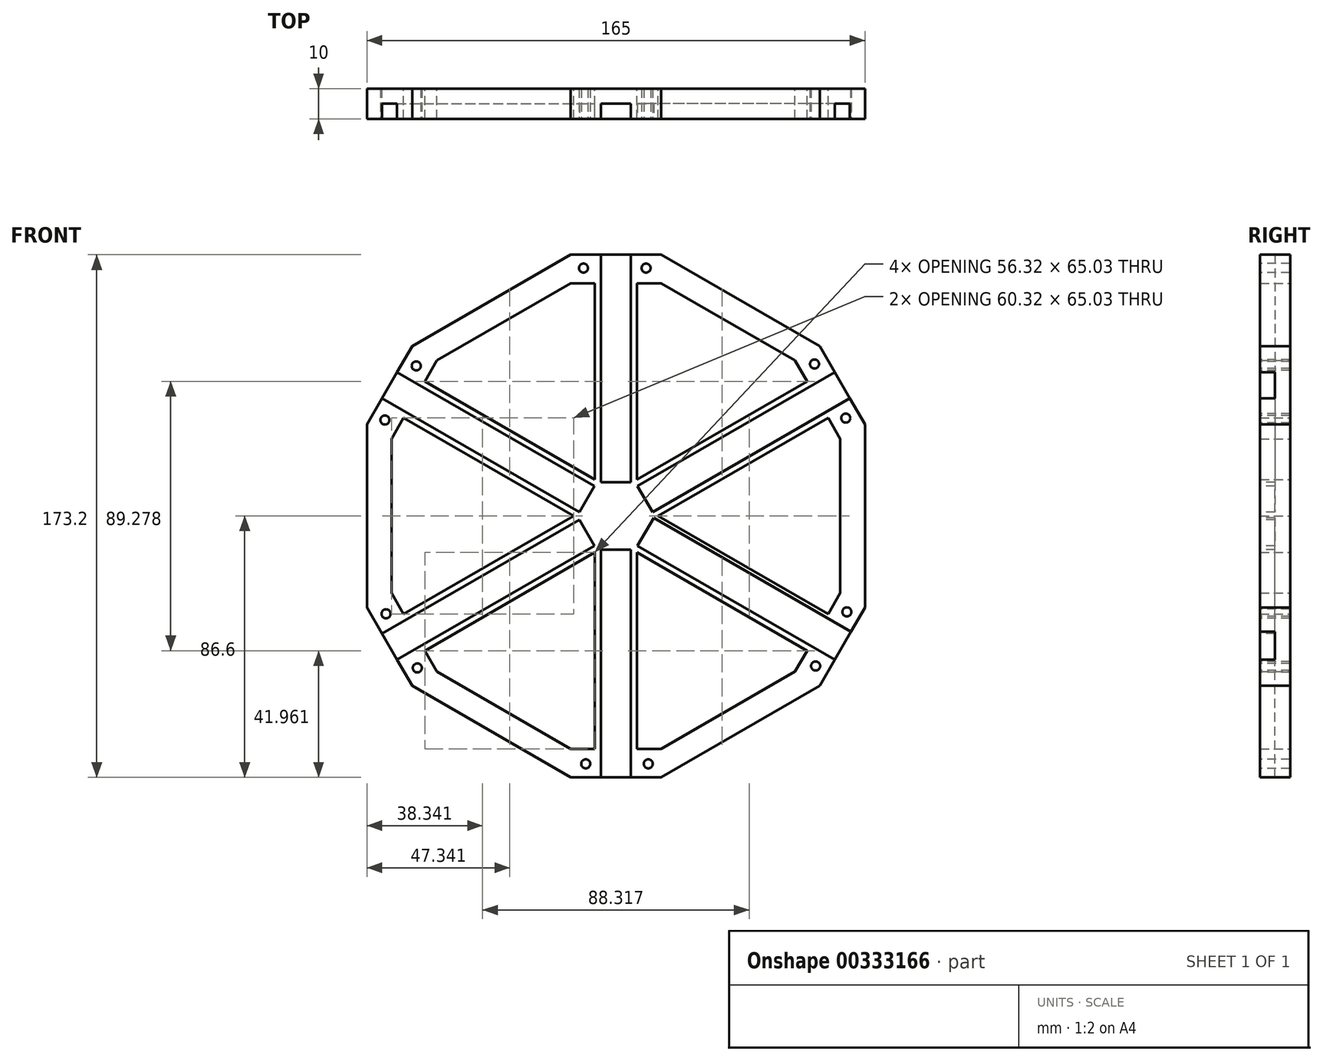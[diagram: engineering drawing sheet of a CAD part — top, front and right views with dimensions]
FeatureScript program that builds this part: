
annotation { "Feature Type Name" : "Feature", "Feature Type Description" : "" }
export const myFeature = defineFeature(function(context is Context, id is Id, definition is map)
    precondition{}
    {
        {
            var Q0;
            Q0=qCreatedBy(makeId("Front.planeOp"),FACE);
            var sketch = newSketch(context, id + "F0", { "sketchPlane" : qUnion([Q0])});
            skCircle(sketch, "E0.cCircle", {"center": v(0, 0) * mm, "radius": 86.6 * mm, "construction": true});
            skLineSegment(sketch, "E0.0", {"start": v(-50, 86.6) * mm, "end": v(50, 86.6) * mm});
            skLineSegment(sketch, "E0.1", {"start": v(50, 86.6) * mm, "end": v(100, 0) * mm});
            skLineSegment(sketch, "E0.2", {"start": v(100, 0) * mm, "end": v(50, -86.6) * mm});
            skLineSegment(sketch, "E0.3", {"start": v(50, -86.6) * mm, "end": v(-50, -86.6) * mm});
            skLineSegment(sketch, "E0.4", {"start": v(-50, -86.6) * mm, "end": v(-100, 0) * mm});
            skLineSegment(sketch, "E0.5", {"start": v(-100, 0) * mm, "end": v(-50, 86.6) * mm});
            skPoint(sketch, "E0.0.midPoint", {"position": v(0, 86.6) * mm});
            skLineSegment(sketch, "E1", {"start": v(-15, 86.6) * mm, "end": v(-15, 77.15) * mm});
            skLineSegment(sketch, "E2", {"start": v(-15, 77.15) * mm, "end": v(-7, 77.15) * mm});
            skLineSegment(sketch, "E3", {"start": v(-7, 77.15) * mm, "end": v(-7, 12.12) * mm});
            skLineSegment(sketch, "E4.MirrorCS", {"start": v(7, 77.15) * mm, "end": v(7, 12.12) * mm});
            skLineSegment(sketch, "E5.MirrorCS", {"start": v(15, 77.15) * mm, "end": v(7, 77.15) * mm});
            skLineSegment(sketch, "E6.MirrorCS", {"start": v(15, 86.6) * mm, "end": v(15, 77.15) * mm});
            skLineSegment(sketch, "E7.1.0", {"start": v(-82.5, 30.31) * mm, "end": v(-74.32, 25.59) * mm});
            skLineSegment(sketch, "E7.1.1", {"start": v(-70.32, 32.51) * mm, "end": v(-14, 0) * mm});
            skLineSegment(sketch, "E7.1.2", {"start": v(-63.32, 44.64) * mm, "end": v(-7, 12.12) * mm});
            skLineSegment(sketch, "E7.1.3", {"start": v(-67.5, 56.3) * mm, "end": v(-59.32, 51.57) * mm});
            skPoint(sketch, "E7.1.4", {"position": v(-75, 43.3) * mm});
            skLineSegment(sketch, "E7.1.5", {"start": v(-74.32, 25.59) * mm, "end": v(-70.32, 32.51) * mm});
            skLineSegment(sketch, "E7.1.6", {"start": v(-59.32, 51.57) * mm, "end": v(-63.32, 44.64) * mm});
            skLineSegment(sketch, "E7.2.0", {"start": v(-67.5, -56.3) * mm, "end": v(-59.32, -51.57) * mm});
            skLineSegment(sketch, "E7.2.1", {"start": v(-63.32, -44.64) * mm, "end": v(-7, -12.12) * mm});
            skLineSegment(sketch, "E7.2.2", {"start": v(-70.32, -32.51) * mm, "end": v(-14, 0) * mm});
            skLineSegment(sketch, "E7.2.3", {"start": v(-82.5, -30.31) * mm, "end": v(-74.32, -25.59) * mm});
            skPoint(sketch, "E7.2.4", {"position": v(-75, -43.3) * mm});
            skLineSegment(sketch, "E7.2.5", {"start": v(-59.32, -51.57) * mm, "end": v(-63.32, -44.64) * mm});
            skLineSegment(sketch, "E7.2.6", {"start": v(-74.32, -25.59) * mm, "end": v(-70.32, -32.51) * mm});
            skLineSegment(sketch, "E7.3.0", {"start": v(15, -86.6) * mm, "end": v(15, -77.15) * mm});
            skLineSegment(sketch, "E7.3.1", {"start": v(7, -77.15) * mm, "end": v(7, -12.12) * mm});
            skLineSegment(sketch, "E7.3.2", {"start": v(-7, -77.15) * mm, "end": v(-7, -12.12) * mm});
            skLineSegment(sketch, "E7.3.3", {"start": v(-15, -86.6) * mm, "end": v(-15, -77.15) * mm});
            skPoint(sketch, "E7.3.4", {"position": v(0, -86.6) * mm});
            skLineSegment(sketch, "E7.3.5", {"start": v(15, -77.15) * mm, "end": v(7, -77.15) * mm});
            skLineSegment(sketch, "E7.3.6", {"start": v(-15, -77.15) * mm, "end": v(-7, -77.15) * mm});
            skLineSegment(sketch, "E7.4.0", {"start": v(82.5, -30.31) * mm, "end": v(74.32, -25.59) * mm});
            skLineSegment(sketch, "E7.4.1", {"start": v(70.32, -32.51) * mm, "end": v(14, 0) * mm});
            skLineSegment(sketch, "E7.4.2", {"start": v(63.32, -44.64) * mm, "end": v(7, -12.12) * mm});
            skLineSegment(sketch, "E7.4.3", {"start": v(67.5, -56.3) * mm, "end": v(59.32, -51.57) * mm});
            skPoint(sketch, "E7.4.4", {"position": v(75, -43.3) * mm});
            skLineSegment(sketch, "E7.4.5", {"start": v(74.32, -25.59) * mm, "end": v(70.32, -32.51) * mm});
            skLineSegment(sketch, "E7.4.6", {"start": v(59.32, -51.57) * mm, "end": v(63.32, -44.64) * mm});
            skLineSegment(sketch, "E7.5.0", {"start": v(67.5, 56.3) * mm, "end": v(59.32, 51.57) * mm});
            skLineSegment(sketch, "E7.5.1", {"start": v(63.32, 44.64) * mm, "end": v(7, 12.12) * mm});
            skLineSegment(sketch, "E7.5.2", {"start": v(70.32, 32.51) * mm, "end": v(14, 0) * mm});
            skLineSegment(sketch, "E7.5.3", {"start": v(82.5, 30.31) * mm, "end": v(74.32, 25.59) * mm});
            skPoint(sketch, "E7.5.4", {"position": v(75, 43.3) * mm});
            skLineSegment(sketch, "E7.5.5", {"start": v(59.32, 51.57) * mm, "end": v(63.32, 44.64) * mm});
            skLineSegment(sketch, "E7.5.6", {"start": v(74.32, 25.59) * mm, "end": v(70.32, 32.51) * mm});
            skPoint(sketch, "E8.orphan", {"position": v(-3.5, 6.06) * mm});
            skPoint(sketch, "E9.orphan", {"position": v(-7, 0) * mm});
            skPoint(sketch, "E10.orphan", {"position": v(3.5, 6.06) * mm});
            skPoint(sketch, "E11.trimOffspring.end.orphan", {"position": v(7, 0) * mm});
            skPoint(sketch, "E12.orphan", {"position": v(3.5, -6.06) * mm});
            skLineSegment(sketch, "E13", {"start": v(-15, -77.15) * mm, "end": v(-59.32, -51.57) * mm});
            skLineSegment(sketch, "E14", {"start": v(-74.32, -25.59) * mm, "end": v(-74.32, 25.59) * mm});
            skLineSegment(sketch, "E15", {"start": v(-59.32, 51.57) * mm, "end": v(-15, 77.15) * mm});
            skLineSegment(sketch, "E16", {"start": v(15, 77.15) * mm, "end": v(59.32, 51.57) * mm});
            skLineSegment(sketch, "E17", {"start": v(74.32, 25.59) * mm, "end": v(74.32, -25.59) * mm});
            skLineSegment(sketch, "E18", {"start": v(59.32, -51.57) * mm, "end": v(15, -77.15) * mm});
            skLineSegment(sketch, "E19", {"start": v(15, -86.6) * mm, "end": v(67.5, -56.3) * mm});
            skLineSegment(sketch, "E20", {"start": v(82.5, -30.31) * mm, "end": v(82.5, 30.31) * mm});
            skLineSegment(sketch, "E21", {"start": v(67.5, 56.3) * mm, "end": v(15, 86.6) * mm});
            skLineSegment(sketch, "E22", {"start": v(-15, 86.6) * mm, "end": v(-67.5, 56.3) * mm});
            skLineSegment(sketch, "E23", {"start": v(-82.5, 30.31) * mm, "end": v(-82.5, -30.31) * mm});
            skLineSegment(sketch, "E24", {"start": v(-67.5, -56.3) * mm, "end": v(-15, -86.6) * mm});
            skSolve(sketch);
        }
        {
            var Q0;
            {var subQ9=sQuery(id+"F0.wireOp",EDGE,"E1");Q0=makeQuery(id+"F0.imprint","IMPRINT",FACE,{"disambiguationData":[TD([[makeQuery(id+"F0.imprint","IMPRINT",EDGE,{"derivedFrom":subQ9}),1.0]])]});}
            var Q1;
            Q1=makeQuery(id+"F0.imprint","IMPRINT",FACE,{"disambiguationData":[TD([[makeQuery(id+"F0.imprint","IMPRINT",EDGE,{"derivedFrom":sQuery(id+"F0.wireOp",EDGE,"E7.2.0")}),-1.0]])]});
            var Q2;
            Q2=makeQuery(id+"F0.imprint","IMPRINT",FACE,{"disambiguationData":[TD([[makeQuery(id+"F0.imprint","IMPRINT",EDGE,{"derivedFrom":sQuery(id+"F0.wireOp",EDGE,"E7.1.0")}),-1.0]])]});
            var Q3;
            Q3=makeQuery(id+"F0.imprint","IMPRINT",FACE,{"disambiguationData":[TD([[makeQuery(id+"F0.imprint","IMPRINT",EDGE,{"derivedFrom":sQuery(id+"F0.wireOp",EDGE,"E1")}),-1.0]])]});
            var Q4;
            Q4=makeQuery(id+"F0.imprint","IMPRINT",FACE,{"disambiguationData":[TD([[makeQuery(id+"F0.imprint","IMPRINT",EDGE,{"derivedFrom":sQuery(id+"F0.wireOp",EDGE,"E6.MirrorCS")}),1.0]])]});
            var Q5;
            Q5=makeQuery(id+"F0.imprint","IMPRINT",FACE,{"disambiguationData":[TD([[makeQuery(id+"F0.imprint","IMPRINT",EDGE,{"derivedFrom":sQuery(id+"F0.wireOp",EDGE,"E7.4.0")}),-1.0]])]});
            var Q6;
            Q6=makeQuery(id+"F0.imprint","IMPRINT",FACE,{"disambiguationData":[TD([[makeQuery(id+"F0.imprint","IMPRINT",EDGE,{"derivedFrom":sQuery(id+"F0.wireOp",EDGE,"E7.3.0")}),-1.0]])]});
            extrude(context, id + "F1", {"entities" : qUnion([Q0, Q1, Q2, Q3, Q4, Q5, Q6]), "depth" : 10 * mm});
        }
        {
            var Q0;
            Q0=makeQuery(id+"F1.opExtrude","CAP_FACE",FACE,{"disambiguationData":[OSD([sQuery(id+"F0.wireOp",EDGE,"E0.0"),sQuery(id+"F0.wireOp",EDGE,"E0.1"),sQuery(id+"F0.wireOp",EDGE,"E0.2"),sQuery(id+"F0.wireOp",EDGE,"E0.3"),sQuery(id+"F0.wireOp",EDGE,"E0.4"),sQuery(id+"F0.wireOp",EDGE,"E0.5"),sQuery(id+"F0.wireOp",EDGE,"E1"),sQuery(id+"F0.wireOp",EDGE,"E2"),sQuery(id+"F0.wireOp",EDGE,"E3"),sQuery(id+"F0.wireOp",EDGE,"E4.MirrorCS"),sQuery(id+"F0.wireOp",EDGE,"E5.MirrorCS"),sQuery(id+"F0.wireOp",EDGE,"E6.MirrorCS"),sQuery(id+"F0.wireOp",EDGE,"E7.1.0"),sQuery(id+"F0.wireOp",EDGE,"E7.1.1"),sQuery(id+"F0.wireOp",EDGE,"E7.1.2"),sQuery(id+"F0.wireOp",EDGE,"E7.1.3"),sQuery(id+"F0.wireOp",EDGE,"E7.1.5"),sQuery(id+"F0.wireOp",EDGE,"E7.1.6"),sQuery(id+"F0.wireOp",EDGE,"E7.2.0"),sQuery(id+"F0.wireOp",EDGE,"E7.2.1"),sQuery(id+"F0.wireOp",EDGE,"E7.2.2"),sQuery(id+"F0.wireOp",EDGE,"E7.2.3"),sQuery(id+"F0.wireOp",EDGE,"E7.2.5"),sQuery(id+"F0.wireOp",EDGE,"E7.2.6"),sQuery(id+"F0.wireOp",EDGE,"E7.3.0"),sQuery(id+"F0.wireOp",EDGE,"E7.3.1"),sQuery(id+"F0.wireOp",EDGE,"E7.3.2"),sQuery(id+"F0.wireOp",EDGE,"E7.3.3"),sQuery(id+"F0.wireOp",EDGE,"E7.3.5"),sQuery(id+"F0.wireOp",EDGE,"E7.3.6"),sQuery(id+"F0.wireOp",EDGE,"E7.4.0"),sQuery(id+"F0.wireOp",EDGE,"E7.4.1"),sQuery(id+"F0.wireOp",EDGE,"E7.4.2"),sQuery(id+"F0.wireOp",EDGE,"E7.4.3"),sQuery(id+"F0.wireOp",EDGE,"E7.4.5"),sQuery(id+"F0.wireOp",EDGE,"E7.4.6"),sQuery(id+"F0.wireOp",EDGE,"E7.5.0"),sQuery(id+"F0.wireOp",EDGE,"E7.5.1"),sQuery(id+"F0.wireOp",EDGE,"E7.5.2"),sQuery(id+"F0.wireOp",EDGE,"E7.5.3"),sQuery(id+"F0.wireOp",EDGE,"E7.5.5"),sQuery(id+"F0.wireOp",EDGE,"E7.5.6")])],"isStart":false});
            var sketch = newSketch(context, id + "F2", { "sketchPlane" : qUnion([Q0])});
            skLineSegment(sketch, "E25.bottom", {"start": v(-5, 86.6) * mm, "end": v(5, 86.6) * mm});
            skLineSegment(sketch, "E25.left", {"start": v(-5, 86.6) * mm, "end": v(-5, 8.66) * mm});
            skLineSegment(sketch, "E25.right", {"start": v(5, 86.6) * mm, "end": v(5, 8.66) * mm});
            skLineSegment(sketch, "E26.1.1", {"start": v(-114.84, 60.53) * mm, "end": v(-10, 0) * mm});
            skLineSegment(sketch, "E26.1.2", {"start": v(-109.84, 69.2) * mm, "end": v(-5, 8.66) * mm});
            skLineSegment(sketch, "E26.1.3", {"start": v(-114.84, 60.53) * mm, "end": v(-109.84, 69.2) * mm});
            skLineSegment(sketch, "E26.2.1", {"start": v(-136.83, -84.77) * mm, "end": v(-5, -8.66) * mm});
            skLineSegment(sketch, "E26.2.2", {"start": v(-141.83, -76.11) * mm, "end": v(-10, 0) * mm});
            skLineSegment(sketch, "E26.2.3", {"start": v(-136.83, -84.77) * mm, "end": v(-141.83, -76.11) * mm});
            skLineSegment(sketch, "E26.3.1", {"start": v(5, -109.05) * mm, "end": v(5, -8.66) * mm});
            skLineSegment(sketch, "E26.3.2", {"start": v(-5, -109.05) * mm, "end": v(-5, -8.66) * mm});
            skLineSegment(sketch, "E26.3.3", {"start": v(5, -109.05) * mm, "end": v(-5, -109.05) * mm});
            skLineSegment(sketch, "E26.4.1", {"start": v(112.24, -58.19) * mm, "end": v(10.73, 0.42) * mm});
            skLineSegment(sketch, "E26.4.2", {"start": v(106.88, -67.48) * mm, "end": v(5, -8.66) * mm});
            skLineSegment(sketch, "E26.4.3", {"start": v(112.24, -58.19) * mm, "end": v(106.88, -67.48) * mm});
            skLineSegment(sketch, "E26.5.1", {"start": v(121.62, 76) * mm, "end": v(5, 8.66) * mm});
            skLineSegment(sketch, "E26.5.2", {"start": v(126.62, 67.33) * mm, "end": v(10.73, 0.42) * mm});
            skLineSegment(sketch, "E26.5.3", {"start": v(121.62, 76) * mm, "end": v(126.62, 67.33) * mm});
            skPoint(sketch, "E26.center", {"position": v(0, 0) * mm});
            skCircle(sketch, "E27.cCircle", {"center": v(0, 0) * mm, "radius": 8.66 * mm, "construction": true});
            skLineSegment(sketch, "E27.0", {"start": v(5, -8.66) * mm, "end": v(-5, -8.66) * mm});
            skLineSegment(sketch, "E27.1", {"start": v(-5, -8.66) * mm, "end": v(-10, 0) * mm});
            skLineSegment(sketch, "E27.2", {"start": v(-10, 0) * mm, "end": v(-5, 8.66) * mm});
            skLineSegment(sketch, "E27.3", {"start": v(-5, 8.66) * mm, "end": v(5, 8.66) * mm});
            skLineSegment(sketch, "E27.4", {"start": v(5, 8.66) * mm, "end": v(10, 0) * mm});
            skLineSegment(sketch, "E27.5", {"start": v(10, 0) * mm, "end": v(5, -8.66) * mm});
            skPoint(sketch, "E27.0.midPoint", {"position": v(0, -8.66) * mm});
            skCircle(sketch, "E28.cCircle", {"center": v(0, 0) * mm, "radius": 11.13 * mm, "construction": true});
            skLineSegment(sketch, "E28.0", {"start": v(6.42, -11.13) * mm, "end": v(-6.42, -11.13) * mm});
            skLineSegment(sketch, "E28.1", {"start": v(-6.42, -11.13) * mm, "end": v(-12.85, 0) * mm});
            skLineSegment(sketch, "E28.2", {"start": v(-12.85, 0) * mm, "end": v(-6.42, 11.13) * mm});
            skLineSegment(sketch, "E28.3", {"start": v(-6.42, 11.13) * mm, "end": v(6.42, 11.13) * mm});
            skLineSegment(sketch, "E28.4", {"start": v(6.42, 11.13) * mm, "end": v(12.85, 0) * mm});
            skLineSegment(sketch, "E28.5", {"start": v(12.85, 0) * mm, "end": v(6.42, -11.13) * mm});
            skPoint(sketch, "E28.0.midPoint", {"position": v(0, -11.13) * mm});
            skSolve(sketch);
        }
        {
            var Q0;
            {var subQ0=sQuery(id+"F2.wireOp",EDGE,"E26.1.3");Q0=makeQuery(id+"F2.imprint","IMPRINT",FACE,{"disambiguationData":[TD([[makeQuery(id+"F2.imprint","IMPRINT",EDGE,{"derivedFrom":subQ0}),-1.0]])]});}
            var Q1;
            {var subQ0=sQuery(id+"F2.wireOp",EDGE,"E25.bottom");Q1=makeQuery(id+"F2.imprint","IMPRINT",FACE,{"disambiguationData":[TD([[makeQuery(id+"F2.imprint","IMPRINT",EDGE,{"derivedFrom":subQ0}),-1.0]])]});}
            var Q2;
            {var subQ0=sQuery(id+"F2.wireOp",EDGE,"E26.5.3");Q2=makeQuery(id+"F2.imprint","IMPRINT",FACE,{"disambiguationData":[TD([[makeQuery(id+"F2.imprint","IMPRINT",EDGE,{"derivedFrom":subQ0}),-1.0]])]});}
            var Q3;
            {var subQ0=sQuery(id+"F2.wireOp",EDGE,"E26.4.3");Q3=makeQuery(id+"F2.imprint","IMPRINT",FACE,{"disambiguationData":[TD([[makeQuery(id+"F2.imprint","IMPRINT",EDGE,{"derivedFrom":subQ0}),-1.0]])]});}
            var Q4;
            {var subQ0=sQuery(id+"F2.wireOp",EDGE,"E26.3.3");Q4=makeQuery(id+"F2.imprint","IMPRINT",FACE,{"disambiguationData":[TD([[makeQuery(id+"F2.imprint","IMPRINT",EDGE,{"derivedFrom":subQ0}),-1.0]])]});}
            var Q5;
            {var subQ0=sQuery(id+"F2.wireOp",EDGE,"E26.2.3");Q5=makeQuery(id+"F2.imprint","IMPRINT",FACE,{"disambiguationData":[TD([[makeQuery(id+"F2.imprint","IMPRINT",EDGE,{"derivedFrom":subQ0}),-1.0]])]});}
            var Q6;
            {var subQ0=sQuery(id+"F2.wireOp",EDGE,"E28.0");var subQ1=sQuery(id+"F2.wireOp",EDGE,"E26.3.1");var subQ2=makeQuery(id+"F2.imprint","INTERSECT",VERTEX,{"derivedFrom":[subQ1,subQ0]});Q6=makeQuery(id+"F2.imprint","IMPRINT",FACE,{"disambiguationData":[TD([[makeQuery(id+"F2.imprint","IMPRINT",EDGE,{"disambiguationData":[TD([[subQ2,1.0]])],"derivedFrom":subQ1}),1.0]])]});}
            var Q7;
            {var subQ0=sQuery(id+"F2.wireOp",EDGE,"E28.1");var subQ1=sQuery(id+"F2.wireOp",EDGE,"E26.2.1");var subQ2=makeQuery(id+"F2.imprint","INTERSECT",VERTEX,{"derivedFrom":[subQ1,subQ0]});Q7=makeQuery(id+"F2.imprint","IMPRINT",FACE,{"disambiguationData":[TD([[makeQuery(id+"F2.imprint","IMPRINT",EDGE,{"disambiguationData":[TD([[subQ2,1.0]])],"derivedFrom":subQ1}),1.0]])]});}
            var Q8;
            {var subQ0=sQuery(id+"F2.wireOp",EDGE,"E28.2");var subQ1=sQuery(id+"F2.wireOp",EDGE,"E26.1.1");var subQ2=makeQuery(id+"F2.imprint","INTERSECT",VERTEX,{"derivedFrom":[subQ1,subQ0]});Q8=makeQuery(id+"F2.imprint","IMPRINT",FACE,{"disambiguationData":[TD([[makeQuery(id+"F2.imprint","IMPRINT",EDGE,{"disambiguationData":[TD([[subQ2,1.0]])],"derivedFrom":subQ1}),1.0]])]});}
            var Q9;
            {var subQ0=sQuery(id+"F2.wireOp",EDGE,"E28.4");var subQ1=sQuery(id+"F2.wireOp",EDGE,"E26.5.1");var subQ2=makeQuery(id+"F2.imprint","INTERSECT",VERTEX,{"derivedFrom":[subQ1,subQ0]});Q9=makeQuery(id+"F2.imprint","IMPRINT",FACE,{"disambiguationData":[TD([[makeQuery(id+"F2.imprint","IMPRINT",EDGE,{"disambiguationData":[TD([[subQ2,1.0]])],"derivedFrom":subQ1}),1.0]])]});}
            var Q10;
            {var subQ0=sQuery(id+"F2.wireOp",EDGE,"E28.5");var subQ1=sQuery(id+"F2.wireOp",EDGE,"E26.4.1");var subQ2=makeQuery(id+"F2.imprint","INTERSECT",VERTEX,{"derivedFrom":[subQ1,subQ0]});Q10=makeQuery(id+"F2.imprint","IMPRINT",FACE,{"disambiguationData":[TD([[makeQuery(id+"F2.imprint","IMPRINT",EDGE,{"disambiguationData":[TD([[subQ2,1.0]])],"derivedFrom":subQ1}),1.0]])]});}
            extrude(context, id + "F3", {"entities" : qUnion([Q0, Q1, Q2, Q3, Q4, Q5, Q6, Q7, Q8, Q9, Q10]), "operationType" : NewBodyOperationType.REMOVE, "oppositeDirection" : true, "depth" : 5 * mm});
        }
        {
            var Q0;
            Q0=makeQuery(id+"F1.opExtrude","CAP_FACE",FACE,{"disambiguationData":[OSD([sQuery(id+"F0.wireOp",EDGE,"E0.0"),sQuery(id+"F0.wireOp",EDGE,"E0.1"),sQuery(id+"F0.wireOp",EDGE,"E0.2"),sQuery(id+"F0.wireOp",EDGE,"E0.3"),sQuery(id+"F0.wireOp",EDGE,"E0.4"),sQuery(id+"F0.wireOp",EDGE,"E0.5"),sQuery(id+"F0.wireOp",EDGE,"E1"),sQuery(id+"F0.wireOp",EDGE,"E2"),sQuery(id+"F0.wireOp",EDGE,"E3"),sQuery(id+"F0.wireOp",EDGE,"E4.MirrorCS"),sQuery(id+"F0.wireOp",EDGE,"E5.MirrorCS"),sQuery(id+"F0.wireOp",EDGE,"E6.MirrorCS"),sQuery(id+"F0.wireOp",EDGE,"E7.1.0"),sQuery(id+"F0.wireOp",EDGE,"E7.1.1"),sQuery(id+"F0.wireOp",EDGE,"E7.1.2"),sQuery(id+"F0.wireOp",EDGE,"E7.1.3"),sQuery(id+"F0.wireOp",EDGE,"E7.1.5"),sQuery(id+"F0.wireOp",EDGE,"E7.1.6"),sQuery(id+"F0.wireOp",EDGE,"E7.2.0"),sQuery(id+"F0.wireOp",EDGE,"E7.2.1"),sQuery(id+"F0.wireOp",EDGE,"E7.2.2"),sQuery(id+"F0.wireOp",EDGE,"E7.2.3"),sQuery(id+"F0.wireOp",EDGE,"E7.2.5"),sQuery(id+"F0.wireOp",EDGE,"E7.2.6"),sQuery(id+"F0.wireOp",EDGE,"E7.3.0"),sQuery(id+"F0.wireOp",EDGE,"E7.3.1"),sQuery(id+"F0.wireOp",EDGE,"E7.3.2"),sQuery(id+"F0.wireOp",EDGE,"E7.3.3"),sQuery(id+"F0.wireOp",EDGE,"E7.3.5"),sQuery(id+"F0.wireOp",EDGE,"E7.3.6"),sQuery(id+"F0.wireOp",EDGE,"E7.4.0"),sQuery(id+"F0.wireOp",EDGE,"E7.4.1"),sQuery(id+"F0.wireOp",EDGE,"E7.4.2"),sQuery(id+"F0.wireOp",EDGE,"E7.4.3"),sQuery(id+"F0.wireOp",EDGE,"E7.4.5"),sQuery(id+"F0.wireOp",EDGE,"E7.4.6"),sQuery(id+"F0.wireOp",EDGE,"E7.5.0"),sQuery(id+"F0.wireOp",EDGE,"E7.5.1"),sQuery(id+"F0.wireOp",EDGE,"E7.5.2"),sQuery(id+"F0.wireOp",EDGE,"E7.5.3"),sQuery(id+"F0.wireOp",EDGE,"E7.5.5"),sQuery(id+"F0.wireOp",EDGE,"E7.5.6")])],"isStart":false});
            var sketch = newSketch(context, id + "F4", { "sketchPlane" : qUnion([Q0])});
            skCircle(sketch, "E29", {"center": v(66.15, -49.74) * mm, "radius": 1.5 * mm});
            skLineSegment(sketch, "E30", {"start": v(9.82, -5.25) * mm, "end": v(56.83, -32.39) * mm, "construction": true});
            skCircle(sketch, "E31.MirrorC", {"center": v(76.51, -31.78) * mm, "radius": 1.5 * mm});
            skCircle(sketch, "E32.1.0", {"center": v(76.15, 32.42) * mm, "radius": 1.5 * mm});
            skCircle(sketch, "E32.1.1", {"center": v(65.78, 50.37) * mm, "radius": 1.5 * mm});
            skCircle(sketch, "E32.2.0", {"center": v(10, 82.15) * mm, "radius": 1.5 * mm});
            skCircle(sketch, "E32.2.1", {"center": v(-10.73, 82.15) * mm, "radius": 1.5 * mm});
            skPoint(sketch, "E32.center", {"position": v(0, 0) * mm});
            skCircle(sketch, "E33.1.3.0", {"center": v(-66.15, 49.74) * mm, "radius": 1.5 * mm});
            skCircle(sketch, "E33.2.3.0", {"center": v(-76.51, 31.78) * mm, "radius": 1.5 * mm});
            skCircle(sketch, "E33.1.4.0", {"center": v(-76.15, -32.42) * mm, "radius": 1.5 * mm});
            skCircle(sketch, "E33.2.4.0", {"center": v(-65.78, -50.37) * mm, "radius": 1.5 * mm});
            skCircle(sketch, "E33.1.5.0", {"center": v(-10, -82.15) * mm, "radius": 1.5 * mm});
            skCircle(sketch, "E33.2.5.0", {"center": v(10.73, -82.15) * mm, "radius": 1.5 * mm});
            skSolve(sketch);
        }
        {
            var Q0;
            Q0=qSketchRegion(id+"F4",true);
            extrude(context, id + "F5", {"entities" : qUnion([Q0]), "operationType" : NewBodyOperationType.REMOVE, "oppositeDirection" : true, "depth" : 25 * mm});
        }
    });
